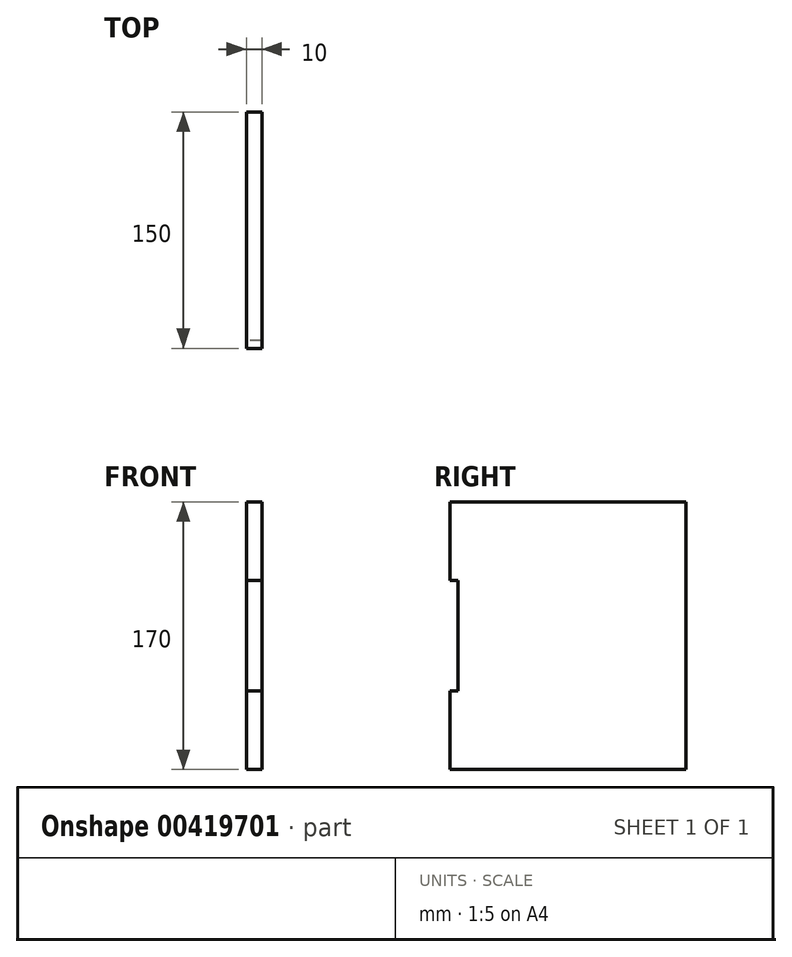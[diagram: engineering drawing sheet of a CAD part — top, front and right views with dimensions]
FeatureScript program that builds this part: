
annotation { "Feature Type Name" : "Feature", "Feature Type Description" : "" }
export const myFeature = defineFeature(function(context is Context, id is Id, definition is map)
    precondition{}
    {
        {
            var Q0;
            Q0=qCreatedBy(makeId("Right.planeOp"),FACE);
            var sketch = newSketch(context, id + "F0", { "sketchPlane" : qUnion([Q0])});
            skLineSegment(sketch, "E0.bottom", {"start": v(74.07, 75.23) * mm, "end": v(-75.93, 75.23) * mm});
            skLineSegment(sketch, "E0.top", {"start": v(74.07, -94.77) * mm, "end": v(-75.93, -94.77) * mm});
            skLineSegment(sketch, "E0.left", {"start": v(74.07, 75.23) * mm, "end": v(74.07, -94.77) * mm});
            skLineSegment(sketch, "E0.right", {"start": v(-75.93, 75.23) * mm, "end": v(-75.93, 25.23) * mm});
            skLineSegment(sketch, "E1.bottom", {"start": v(-75.93, 25.23) * mm, "end": v(-70.93, 25.23) * mm});
            skLineSegment(sketch, "E1.top", {"start": v(-75.93, -44.77) * mm, "end": v(-70.93, -44.77) * mm});
            skLineSegment(sketch, "E1.right", {"start": v(-70.93, 25.23) * mm, "end": v(-70.93, -44.77) * mm});
            skLineSegment(sketch, "E2.trimOffspring", {"start": v(-75.93, -44.77) * mm, "end": v(-75.93, -94.77) * mm});
            skSolve(sketch);
        }
        {
            var Q0;
            Q0=makeQuery(id+"F0.imprint","IMPRINT",FACE,{"disambiguationData":[TD([[makeQuery(id+"F0.imprint","IMPRINT",EDGE,{"derivedFrom":sQuery(id+"F0.wireOp",EDGE,"E0.bottom")}),1.0]])]});
            extrude(context, id + "F1", {"entities" : qUnion([Q0]), "depth" : 10 * mm});
        }
    });
